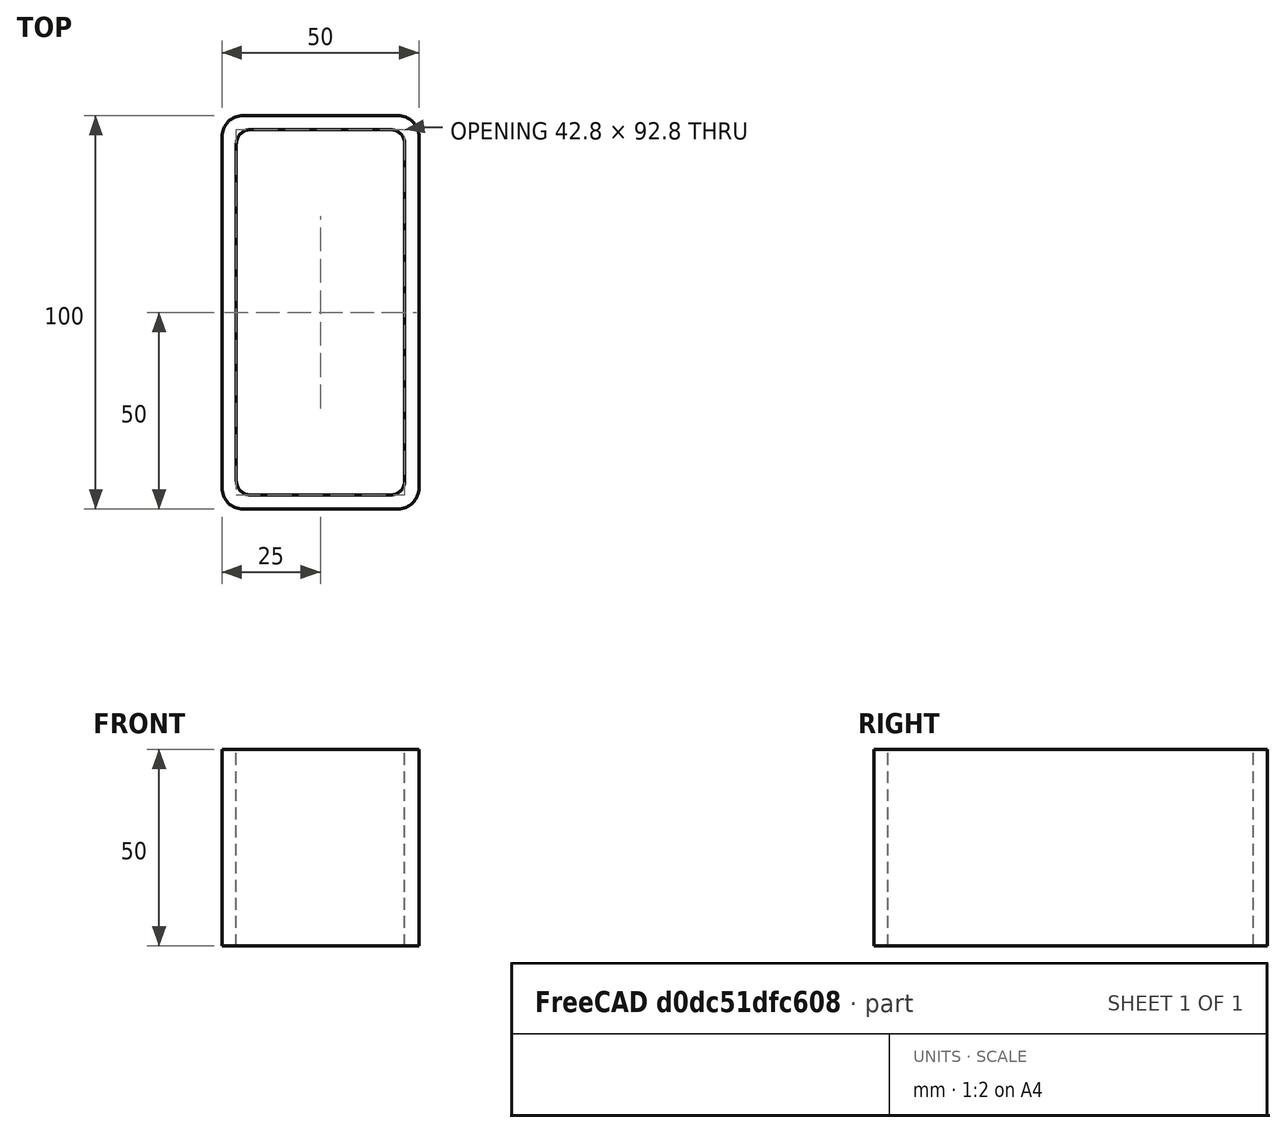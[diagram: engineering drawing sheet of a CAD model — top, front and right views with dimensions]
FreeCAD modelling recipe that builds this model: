
FCSTD DOCUMENT  (FreeCAD 0.15R4671 (Git))
Label: Rectangular hollow section 100x50x3.6 EN10219 S235JRH
License: All rights reserved
LicenseURL: http://en.wikipedia.org/wiki/All_rights_reserved
objects: Sketcher::SketchObject×1, Part::Extrusion×1
note: 2 computed .brp shape members not serialized (recipe doc carries the construction recipe); baked Part::Feature solids carry a one-line shape summary decoded from their .brp

FEATURE [Sketcher::SketchObject] Sketch
  sketch-geometry (16):
    g0: LineSegment StartX=-17.8 StartY=46.4 StartZ=0 EndX=17.8 EndY=46.4 EndZ=0
    g1: LineSegment StartX=21.4 StartY=42.8 StartZ=0 EndX=21.4 EndY=-42.8 EndZ=0
    g2: LineSegment StartX=17.8 StartY=-46.4 StartZ=0 EndX=-17.8 EndY=-46.4 EndZ=0
    g3: LineSegment StartX=-21.4 StartY=-42.8 StartZ=0 EndX=-21.4 EndY=42.8 EndZ=0
    g4: LineSegment StartX=-19.6 StartY=50 StartZ=0 EndX=19.6 EndY=50 EndZ=0
    g5: LineSegment StartX=25 StartY=44.6 StartZ=0 EndX=25 EndY=-44.6 EndZ=0
    g6: LineSegment StartX=19.6 StartY=-50 StartZ=0 EndX=-19.6 EndY=-50 EndZ=0
    g7: LineSegment StartX=-25 StartY=-44.6 StartZ=0 EndX=-25 EndY=44.6 EndZ=0
    g8: ArcOfCircle CenterX=-17.8 CenterY=42.8 CenterZ=0 NormalX=0 NormalY=0 NormalZ=1 Radius=3.6 StartAngle=1.5708 EndAngle=3.14159
    g9: ArcOfCircle CenterX=17.8 CenterY=42.8 CenterZ=0 NormalX=0 NormalY=0 NormalZ=1 Radius=3.6 StartAngle=0 EndAngle=1.5708
    g10: ArcOfCircle CenterX=17.8 CenterY=-42.8 CenterZ=0 NormalX=0 NormalY=0 NormalZ=1 Radius=3.6 StartAngle=4.71239 EndAngle=6.28319
    g11: ArcOfCircle CenterX=-17.8 CenterY=-42.8 CenterZ=0 NormalX=0 NormalY=0 NormalZ=1 Radius=3.6 StartAngle=3.14159 EndAngle=4.71239
    g12: ArcOfCircle CenterX=19.6 CenterY=44.6 CenterZ=0 NormalX=0 NormalY=0 NormalZ=1 Radius=5.4 StartAngle=0 EndAngle=1.5708
    g13: ArcOfCircle CenterX=19.6 CenterY=-44.6 CenterZ=0 NormalX=0 NormalY=0 NormalZ=1 Radius=5.4 StartAngle=4.71239 EndAngle=6.28319
    g14: ArcOfCircle CenterX=-19.6 CenterY=-44.6 CenterZ=0 NormalX=0 NormalY=0 NormalZ=1 Radius=5.4 StartAngle=3.14159 EndAngle=4.71239
    g15: ArcOfCircle CenterX=-19.6 CenterY=44.6 CenterZ=0 NormalX=0 NormalY=0 NormalZ=1 Radius=5.4 StartAngle=1.5708 EndAngle=3.14159
  constraints (36):
    c: Horizontal(g2)
    c: Vertical(g3)
    c: Horizontal(g6)
    c: Vertical(g7)
    c: Tangent(g3,g8) = 1.5708
    c: Tangent(g0,g8) = 1.5708
    c: Tangent(g0,g9) = 1.5708
    c: Tangent(g1,g9) = 1.5708
    c: Tangent(g1,g10) = 1.5708
    c: Tangent(g2,g10) = 1.5708
    c: Tangent(g2,g11) = 1.5708
    c: Tangent(g3,g11) = 1.5708
    c: Tangent(g4,g12) = 1.5708
    c: Tangent(g5,g12) = 1.5708
    c: Tangent(g5,g13) = 1.5708
    c: Tangent(g6,g13) = 1.5708
    c: Tangent(g6,g14) = 1.5708
    c: Tangent(g7,g14) = 1.5708
    c: Tangent(g7,g15) = 1.5708
    c: Tangent(g4,g15) = 1.5708
    c: Equal(g9,g8)
    c: Equal(g9,g11)
    c: Equal(g9,g10)
    c: Equal(g12,g15)
    c: Equal(g12,g14)
    c: Equal(g12,g13)
    c: Symmetric(g4,g6,g-1)
    c: Symmetric(g7,g5,g-2)
    c: DistanceY(g4,g6) = -100
    c: DistanceX(g7,g5) = 50
    c: Symmetric(g3,g1,g-2)
    c: Symmetric(g0,g2,g-1)
    c: DistanceY(g0,g4) = 3.6
    c: DistanceX(g5,g1) = -3.6
    c: Radius(g9) = 3.6
    c: Radius(g12) = 5.4
FEATURE [Part::Extrusion] Extrude  label="Rectangular hollow section 100x50x3.6 EN10219 S235JRH"
  Base = -> Sketch
  Dir = (0,0,50)
  Solid = true
